# Revit family: 4605600
name_source: partatom
category: Aparatos sanitarios
revit_build: Autodesk Revit 2018 (Build: 20170223_1515(x64)
units: mm (PartAtom-declared; Revit-internal decimal feet)

## family parameters
Anfitrión = Cara
Compartido = No
Corte con vacíos al cargar = No
Cota de conector redondo = Diámetro de uso
Número OmniClass = 23.45.55.14
Punto de cálculo de habitación = No
Tipo de pieza = Normal
Título OmniClass = Single Faucets

## types (1)
- 4605600
    Accionamiento = Mediante maneta
    CAUDAL = 12 l/min
    CIERRE = Mediante maneta
Mediante maneta
    Comentarios de tipo = Temperatura admisible de agua: los materiales que componen las piezas de los grifos pueden soportar una temperatura máxima de 70ºC. Grifo fabricado en latón con acabado cromado. Presión mínima de uso: 0,5 bar. Accionamiento mediante maneta. Cuerpo frio. Rociador de Ø250 de ABS cromado. Maneral de Ø100 mm. y 3 funciones. Caudal de 11,9 l/min de 3 bar y máxima apertura. Entradas hembra de 3/4" a 1/2" con excéntrica y embellecedor. Selección de salidas mediante inversor. Columna no regulable en altura.
    Conexión AC = Sí
    Conexión AF = Sí
    Código de montaje = C1030220
    Descripción = Grifo monomando lavaboo para instalación en mural
    ENTRADA = Hembra de 3/4" a 1/2" con exentrica y embellecedor.
    Elevación por defecto = 1219 mm
    Fabricante = PRESTO IBÉRICA
    Imagen de tipo = <Ninguno>
    Material = LATON CROMADO
    Modelo = AROHA lavabo mural
    Presión Máxima = 3 bar
    REFERENCIA = 4605600
    TIPO DE AGUA = Fria/Caliente
    Teléfono = (+34) 915 782 575
    URL = http://www.griferiasgalindo.com
